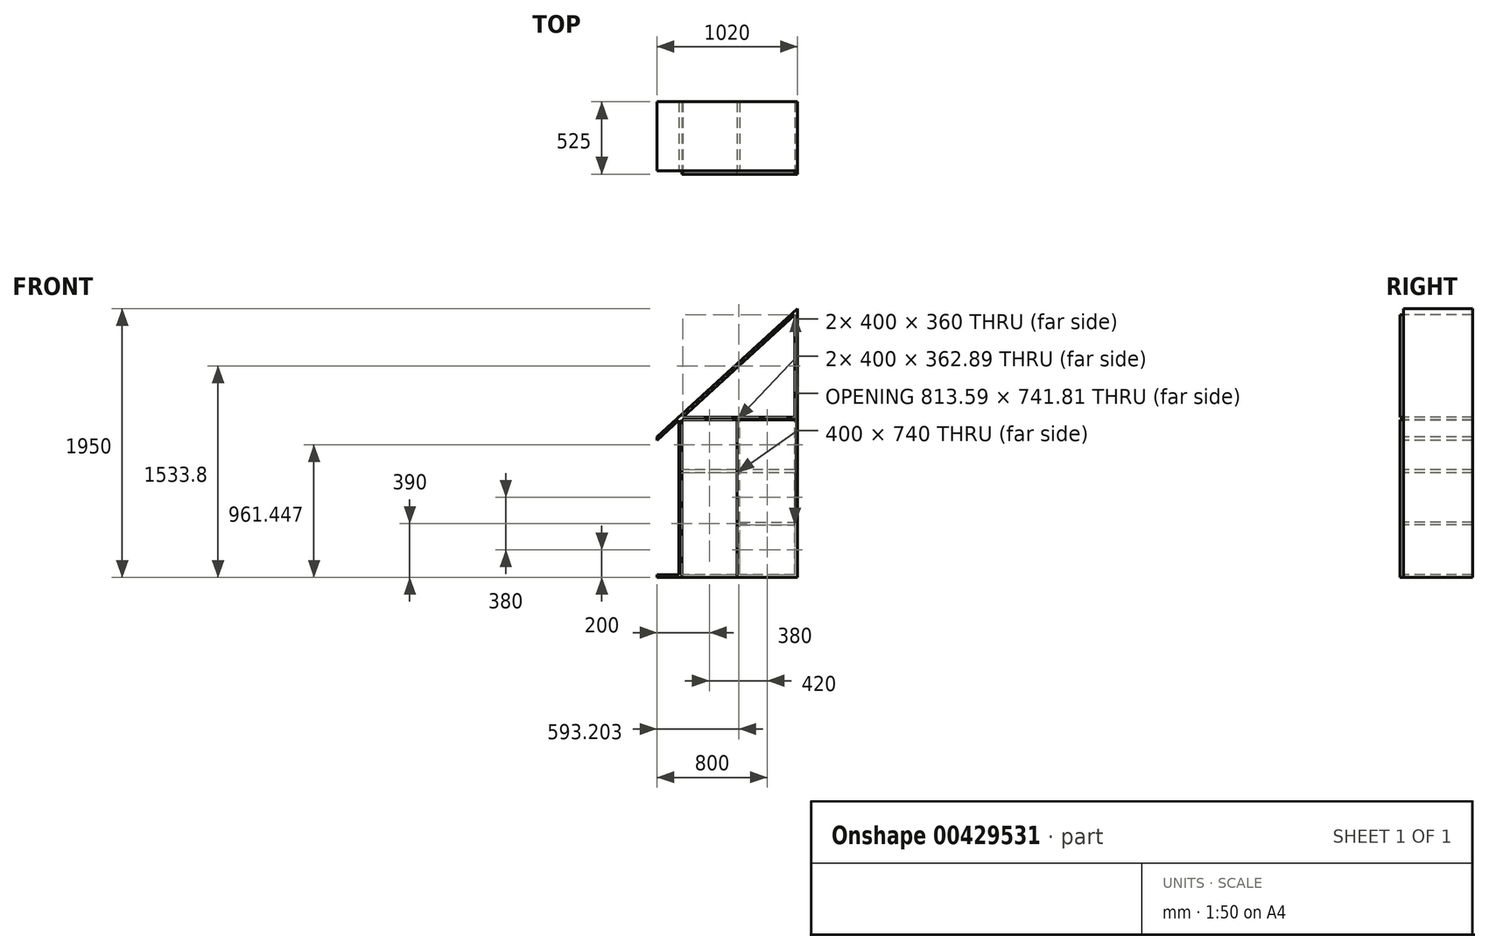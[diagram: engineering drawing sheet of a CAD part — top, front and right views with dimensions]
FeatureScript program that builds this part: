
annotation { "Feature Type Name" : "Feature", "Feature Type Description" : "" }
export const myFeature = defineFeature(function(context is Context, id is Id, definition is map)
    precondition{}
    {
        {
            var Q0;
            Q0=qCreatedBy(makeId("Front.planeOp"),FACE);
            var sketch = newSketch(context, id + "F0", { "sketchPlane" : qUnion([Q0])});
            skLineSegment(sketch, "E0.bottom", {"start": v(510, -975) * mm, "end": v(-510, -975) * mm});
            skLineSegment(sketch, "E0.left", {"start": v(510, -975) * mm, "end": v(510, 975) * mm});
            skLineSegment(sketch, "E0.right", {"start": v(-510, -975) * mm, "end": v(-510, 45) * mm});
            skPoint(sketch, "E0.middle", {"position": v(0, 180) * mm});
            skLineSegment(sketch, "E1", {"start": v(-510, 45) * mm, "end": v(510, 975) * mm});
            skLineSegment(sketch, "E2.0", {"start": v(-350, -975) * mm, "end": v(-350, 190.88) * mm});
            skPoint(sketch, "E0.top.end.orphan", {"position": v(-510, 975) * mm});
            skLineSegment(sketch, "E3", {"start": v(-350, 167.9) * mm, "end": v(70, 167.9) * mm});
            skLineSegment(sketch, "E4.0", {"start": v(510, -215) * mm, "end": v(90, -215) * mm});
            skLineSegment(sketch, "E5.0", {"start": v(510, -955) * mm, "end": v(-510, -955) * mm});
            skLineSegment(sketch, "E6.0", {"start": v(-330, -975) * mm, "end": v(-330, 209.12) * mm});
            skLineSegment(sketch, "E7.0", {"start": v(510, -195) * mm, "end": v(90, -195) * mm});
            skLineSegment(sketch, "E8.0", {"start": v(-510, 17.93) * mm, "end": v(510, 947.93) * mm});
            skLineSegment(sketch, "E9.0", {"start": v(90, -975) * mm, "end": v(90, -595) * mm});
            skLineSegment(sketch, "E10.0", {"start": v(70, -975) * mm, "end": v(70, 187.9) * mm});
            skLineSegment(sketch, "E11.0", {"start": v(-330, 187.9) * mm, "end": v(70, 187.9) * mm});
            skLineSegment(sketch, "E12.0", {"start": v(490, -975) * mm, "end": v(490, -595) * mm});
            skLineSegment(sketch, "E13.trimOffspring", {"start": v(70, -195) * mm, "end": v(-350, -195) * mm});
            skLineSegment(sketch, "E14.trimOffspring", {"start": v(70, -215) * mm, "end": v(-350, -215) * mm});
            skLineSegment(sketch, "E15.trimOffspring", {"start": v(90, 187.9) * mm, "end": v(510, 187.9) * mm});
            skLineSegment(sketch, "E16.trimOffspring", {"start": v(90, 167.9) * mm, "end": v(510, 167.9) * mm});
            skLineSegment(sketch, "E17", {"start": v(70, 167.9) * mm, "end": v(90, 167.9) * mm});
            skLineSegment(sketch, "E18", {"start": v(70, 187.9) * mm, "end": v(90, 187.9) * mm});
            skLineSegment(sketch, "E19", {"start": v(90, -575) * mm, "end": v(490, -575) * mm});
            skLineSegment(sketch, "E20", {"start": v(90, -595) * mm, "end": v(490, -595) * mm});
            skLineSegment(sketch, "E21.trimOffspring", {"start": v(90, -575) * mm, "end": v(90, 187.9) * mm});
            skLineSegment(sketch, "E22.trimOffspring", {"start": v(490, -575) * mm, "end": v(490, 956.76) * mm});
            skSolve(sketch);
        }
        {
            var Q0;
            {var subQ0=sQuery(id+"F0.wireOp",EDGE,"E6.0");var subQ1=sQuery(id+"F0.wireOp",EDGE,"E0.bottom");var subQ2=makeQuery(id+"F0.imprint","INTERSECT",VERTEX,{"derivedFrom":[subQ1,subQ0]});Q0=makeQuery(id+"F0.imprint","IMPRINT",FACE,{"disambiguationData":[TD([[makeQuery(id+"F0.imprint","IMPRINT",EDGE,{"disambiguationData":[TD([[subQ2,1.0]])],"derivedFrom":subQ1}),-1.0]])]});}
            var Q1;
            {var subQ0=sQuery(id+"F0.wireOp",EDGE,"E10.0");var subQ1=sQuery(id+"F0.wireOp",EDGE,"6faa854c-3392-4649-b0cb-d51412c366a2.0");var subQ2=makeQuery(id+"F0.imprint","INTERSECT",VERTEX,{"derivedFrom":[subQ1,subQ0]});Q1=makeQuery(id+"F0.imprint","IMPRINT",FACE,{"disambiguationData":[TD([[makeQuery(id+"F0.imprint","IMPRINT",EDGE,{"disambiguationData":[TD([[subQ2,-1.0]])],"derivedFrom":subQ1}),1.0]])]});}
            var Q2;
            {var subQ0=sQuery(id+"F0.wireOp",EDGE,"E10.0");var subQ1=sQuery(id+"F0.wireOp",EDGE,"6faa854c-3392-4649-b0cb-d51412c366a2.0");var subQ2=makeQuery(id+"F0.imprint","INTERSECT",VERTEX,{"derivedFrom":[subQ1,subQ0]});Q2=makeQuery(id+"F0.imprint","IMPRINT",FACE,{"disambiguationData":[TD([[makeQuery(id+"F0.imprint","IMPRINT",EDGE,{"disambiguationData":[TD([[subQ2,-1.0]])],"derivedFrom":subQ1}),-1.0]])]});}
            var Q3;
            {var subQ0=sQuery(id+"F0.wireOp",EDGE,"b3576428-8442-4fca-9c3f-cbccb2f376bd.0");var subQ1=sQuery(id+"F0.wireOp",EDGE,"E6.0");var subQ2=makeQuery(id+"F0.imprint","INTERSECT",VERTEX,{"derivedFrom":[subQ1,subQ0]});Q3=makeQuery(id+"F0.imprint","IMPRINT",FACE,{"disambiguationData":[TD([[makeQuery(id+"F0.imprint","IMPRINT",EDGE,{"disambiguationData":[TD([[subQ2,-1.0]])],"derivedFrom":subQ1}),-1.0]])]});}
            var Q4;
            {var subQ2=sQuery(id+"F0.wireOp",EDGE,"a34f5626-0c33-47cb-b1fa-9412c36bbc4b.0");var subQ8=sQuery(id+"F0.wireOp",EDGE,"E10.0");var subQ9=makeQuery(id+"F0.imprint","INTERSECT",VERTEX,{"derivedFrom":[subQ2,subQ8]});Q4=makeQuery(id+"F0.imprint","IMPRINT",FACE,{"disambiguationData":[TD([[makeQuery(id+"F0.imprint","IMPRINT",EDGE,{"disambiguationData":[TD([[subQ9,-1.0]])],"derivedFrom":subQ2}),-1.0]])]});}
            var Q5;
            {var subQ0=sQuery(id+"F0.wireOp",EDGE,"E10.0");var subQ1=sQuery(id+"F0.wireOp",EDGE,"E3");var subQ2=makeQuery(id+"F0.imprint","INTERSECT",VERTEX,{"derivedFrom":[subQ1,subQ0]});Q5=makeQuery(id+"F0.imprint","IMPRINT",FACE,{"disambiguationData":[TD([[makeQuery(id+"F0.imprint","IMPRINT",EDGE,{"disambiguationData":[TD([[subQ2,1.0]])],"derivedFrom":subQ1}),-1.0]])]});}
            var Q6;
            {var subQ0=sQuery(id+"F0.wireOp",EDGE,"E14.trimOffspring");var subQ1=sQuery(id+"F0.wireOp",EDGE,"E6.0");var subQ2=makeQuery(id+"F0.imprint","INTERSECT",VERTEX,{"derivedFrom":[subQ1,subQ0]});Q6=makeQuery(id+"F0.imprint","IMPRINT",FACE,{"disambiguationData":[TD([[makeQuery(id+"F0.imprint","IMPRINT",EDGE,{"disambiguationData":[TD([[subQ2,-1.0]])],"derivedFrom":subQ1}),-1.0]])]});}
            var Q7;
            {var subQ0=sQuery(id+"F0.wireOp",EDGE,"E10.0");var subQ1=sQuery(id+"F0.wireOp",EDGE,"E5.0");var subQ2=makeQuery(id+"F0.imprint","INTERSECT",VERTEX,{"derivedFrom":[subQ1,subQ0]});Q7=makeQuery(id+"F0.imprint","IMPRINT",FACE,{"disambiguationData":[TD([[makeQuery(id+"F0.imprint","IMPRINT",EDGE,{"disambiguationData":[TD([[subQ2,-1.0]])],"derivedFrom":subQ1}),-1.0]])]});}
            extrude(context, id + "F1", {"entities" : qUnion([Q0, Q1, Q2, Q3, Q4, Q5, Q6, Q7]), "depth" : 25 * mm});
        }
        {
            var Q0;
            {var subQ0=sQuery(id+"F0.wireOp",EDGE,"E9.0");var subQ1=sQuery(id+"F0.wireOp",EDGE,"E0.bottom");var subQ2=makeQuery(id+"F0.imprint","INTERSECT",VERTEX,{"derivedFrom":[subQ1,subQ0]});Q0=makeQuery(id+"F0.imprint","IMPRINT",FACE,{"disambiguationData":[TD([[makeQuery(id+"F0.imprint","IMPRINT",EDGE,{"disambiguationData":[TD([[subQ2,1.0]])],"derivedFrom":subQ1}),-1.0]])]});}
            var Q1;
            {var subQ0=sQuery(id+"F0.wireOp",EDGE,"E9.0");var subQ1=sQuery(id+"F0.wireOp",EDGE,"E4.0");var subQ2=makeQuery(id+"F0.imprint","INTERSECT",VERTEX,{"derivedFrom":[subQ1,subQ0]});Q1=makeQuery(id+"F0.imprint","IMPRINT",FACE,{"disambiguationData":[TD([[makeQuery(id+"F0.imprint","IMPRINT",EDGE,{"disambiguationData":[TD([[subQ2,1.0]])],"derivedFrom":subQ1}),1.0]])]});}
            var Q2;
            {var subQ0=sQuery(id+"F0.wireOp",EDGE,"E9.0");var subQ1=sQuery(id+"F0.wireOp",EDGE,"E7.0");var subQ2=makeQuery(id+"F0.imprint","INTERSECT",VERTEX,{"derivedFrom":[subQ1,subQ0]});Q2=makeQuery(id+"F0.imprint","IMPRINT",FACE,{"disambiguationData":[TD([[makeQuery(id+"F0.imprint","IMPRINT",EDGE,{"disambiguationData":[TD([[subQ2,1.0]])],"derivedFrom":subQ1}),-1.0]])]});}
            var Q3;
            {var subQ0=sQuery(id+"F0.wireOp",EDGE,"E9.0");var subQ1=sQuery(id+"F0.wireOp",EDGE,"E4.0");var subQ2=makeQuery(id+"F0.imprint","INTERSECT",VERTEX,{"derivedFrom":[subQ1,subQ0]});Q3=makeQuery(id+"F0.imprint","IMPRINT",FACE,{"disambiguationData":[TD([[makeQuery(id+"F0.imprint","IMPRINT",EDGE,{"disambiguationData":[TD([[subQ2,1.0]])],"derivedFrom":subQ1}),-1.0]])]});}
            var Q4;
            {var subQ0=sQuery(id+"F0.wireOp",EDGE,"E17");Q4=makeQuery(id+"F0.imprint","IMPRINT",FACE,{"disambiguationData":[TD([[makeQuery(id+"F0.imprint","IMPRINT",EDGE,{"derivedFrom":subQ0}),-1.0]])]});}
            var Q5;
            {var subQ5=sQuery(id+"F0.wireOp",EDGE,"E20");Q5=makeQuery(id+"F0.imprint","IMPRINT",FACE,{"disambiguationData":[TD([[makeQuery(id+"F0.imprint","IMPRINT",EDGE,{"derivedFrom":subQ5}),-1.0]])]});}
            var Q6;
            {var subQ0=sQuery(id+"F0.wireOp",EDGE,"E9.0");var subQ1=sQuery(id+"F0.wireOp",EDGE,"E0.bottom");var subQ2=makeQuery(id+"F0.imprint","INTERSECT",VERTEX,{"derivedFrom":[subQ1,subQ0]});Q6=makeQuery(id+"F0.imprint","IMPRINT",FACE,{"disambiguationData":[TD([[makeQuery(id+"F0.imprint","IMPRINT",EDGE,{"disambiguationData":[TD([[subQ2,-1.0]])],"derivedFrom":subQ1}),-1.0]])]});}
            var Q7;
            {var subQ0=sQuery(id+"F0.wireOp",EDGE,"E0.left");var subQ1=sQuery(id+"F0.wireOp",EDGE,"E0.bottom");var subQ2=makeQuery(id+"F0.imprint","INTERSECT",VERTEX,{"derivedFrom":[subQ1,subQ0]});Q7=makeQuery(id+"F0.imprint","IMPRINT",FACE,{"disambiguationData":[TD([[makeQuery(id+"F0.imprint","IMPRINT",EDGE,{"disambiguationData":[TD([[subQ2,-1.0]])],"derivedFrom":subQ1}),-1.0]])]});}
            extrude(context, id + "F2", {"entities" : qUnion([Q0, Q1, Q2, Q3, Q4, Q5, Q6, Q7]), "depth" : 25 * mm});
        }
        {
            var Q0;
            {var subQ0=sQuery(id+"F0.wireOp",EDGE,"E9.0");var subQ1=sQuery(id+"F0.wireOp",EDGE,"E0.bottom");var subQ2=makeQuery(id+"F0.imprint","INTERSECT",VERTEX,{"derivedFrom":[subQ1,subQ0]});Q0=makeQuery(id+"F0.imprint","IMPRINT",FACE,{"disambiguationData":[TD([[makeQuery(id+"F0.imprint","IMPRINT",EDGE,{"disambiguationData":[TD([[subQ2,1.0]])],"derivedFrom":subQ1}),-1.0]])]});}
            var Q1;
            {var subQ0=sQuery(id+"F0.wireOp",EDGE,"E8.0");var subQ1=sQuery(id+"F0.wireOp",EDGE,"E0.left");var subQ2=makeQuery(id+"F0.imprint","INTERSECT",VERTEX,{"derivedFrom":[subQ1,subQ0]});Q1=makeQuery(id+"F0.imprint","IMPRINT",FACE,{"disambiguationData":[TD([[makeQuery(id+"F0.imprint","IMPRINT",EDGE,{"disambiguationData":[TD([[subQ2,1.0]])],"derivedFrom":subQ1}),1.0]])]});}
            var Q2;
            {var subQ1=sQuery(id+"F0.wireOp",EDGE,"E6.0");var subQ7=sQuery(id+"F0.wireOp",EDGE,"E1");var subQ8=makeQuery(id+"F0.imprint","INTERSECT",VERTEX,{"derivedFrom":[subQ7,subQ1]});Q2=makeQuery(id+"F0.imprint","IMPRINT",FACE,{"disambiguationData":[TD([[makeQuery(id+"F0.imprint","IMPRINT",EDGE,{"disambiguationData":[TD([[subQ8,-1.0]])],"derivedFrom":subQ7}),-1.0]])]});}
            var Q3;
            {var subQ0=sQuery(id+"F0.wireOp",EDGE,"E15.trimOffspring");var subQ1=sQuery(id+"F0.wireOp",EDGE,"E0.left");var subQ2=makeQuery(id+"F0.imprint","INTERSECT",VERTEX,{"derivedFrom":[subQ1,subQ0]});Q3=makeQuery(id+"F0.imprint","IMPRINT",FACE,{"disambiguationData":[TD([[makeQuery(id+"F0.imprint","IMPRINT",EDGE,{"disambiguationData":[TD([[subQ2,1.0]])],"derivedFrom":subQ1}),1.0]])]});}
            var Q4;
            {var subQ0=sQuery(id+"F0.wireOp",EDGE,"E17");Q4=makeQuery(id+"F0.imprint","IMPRINT",FACE,{"disambiguationData":[TD([[makeQuery(id+"F0.imprint","IMPRINT",EDGE,{"derivedFrom":subQ0}),1.0]])]});}
            var Q5;
            {var subQ1=sQuery(id+"F0.wireOp",EDGE,"E6.0");var subQ7=sQuery(id+"F0.wireOp",EDGE,"E3");var subQ8=makeQuery(id+"F0.imprint","INTERSECT",VERTEX,{"derivedFrom":[subQ7,subQ1]});Q5=makeQuery(id+"F0.imprint","IMPRINT",FACE,{"disambiguationData":[TD([[makeQuery(id+"F0.imprint","IMPRINT",EDGE,{"disambiguationData":[TD([[subQ8,-1.0]])],"derivedFrom":subQ1}),-1.0]])]});}
            var Q6;
            {var subQ1=sQuery(id+"F0.wireOp",EDGE,"E2.0");var subQ7=sQuery(id+"F0.wireOp",EDGE,"E1");var subQ8=makeQuery(id+"F0.imprint","INTERSECT",VERTEX,{"derivedFrom":[subQ7,subQ1]});Q6=makeQuery(id+"F0.imprint","IMPRINT",FACE,{"disambiguationData":[TD([[makeQuery(id+"F0.imprint","IMPRINT",EDGE,{"disambiguationData":[TD([[subQ8,-1.0]])],"derivedFrom":subQ7}),-1.0]])]});}
            var Q7;
            {var subQ0=sQuery(id+"F0.wireOp",EDGE,"E8.0");var subQ1=sQuery(id+"F0.wireOp",EDGE,"E3");var subQ2=makeQuery(id+"F0.imprint","INTERSECT",VERTEX,{"derivedFrom":[subQ1,subQ0]});Q7=makeQuery(id+"F0.imprint","IMPRINT",FACE,{"disambiguationData":[TD([[makeQuery(id+"F0.imprint","IMPRINT",EDGE,{"disambiguationData":[TD([[subQ2,-1.0]])],"derivedFrom":subQ1}),1.0]])]});}
            var Q8;
            {var subQ0=sQuery(id+"F0.wireOp",EDGE,"E11.0");var subQ1=sQuery(id+"F0.wireOp",EDGE,"E6.0");var subQ2=makeQuery(id+"F0.imprint","INTERSECT",VERTEX,{"derivedFrom":[subQ1,subQ0]});Q8=makeQuery(id+"F0.imprint","IMPRINT",FACE,{"disambiguationData":[TD([[makeQuery(id+"F0.imprint","IMPRINT",EDGE,{"disambiguationData":[TD([[subQ2,1.0]])],"derivedFrom":subQ1}),-1.0]])]});}
            var Q9;
            {var subQ0=sQuery(id+"F0.wireOp",EDGE,"E3");var subQ1=sQuery(id+"F0.wireOp",EDGE,"E2.0");var subQ2=makeQuery(id+"F0.imprint","INTERSECT",VERTEX,{"derivedFrom":[subQ1,subQ0]});Q9=makeQuery(id+"F0.imprint","IMPRINT",FACE,{"disambiguationData":[TD([[makeQuery(id+"F0.imprint","IMPRINT",EDGE,{"disambiguationData":[TD([[subQ2,1.0]])],"derivedFrom":subQ1}),-1.0]])]});}
            var Q10;
            {var subQ4=sQuery(id+"F0.wireOp",EDGE,"E0.right");var subQ6=sQuery(id+"F0.wireOp",EDGE,"E1");var subQ7=makeQuery(id+"F0.imprint","INTERSECT",VERTEX,{"derivedFrom":[subQ4,subQ6]});Q10=makeQuery(id+"F0.imprint","IMPRINT",FACE,{"disambiguationData":[TD([[makeQuery(id+"F0.imprint","IMPRINT",EDGE,{"disambiguationData":[TD([[subQ7,1.0]])],"derivedFrom":subQ4}),-1.0]])]});}
            var Q11;
            {var subQ3=sQuery(id+"F0.wireOp",EDGE,"E13.trimOffspring");var subQ6=sQuery(id+"F0.wireOp",EDGE,"E2.0");var subQ9=makeQuery(id+"F0.imprint","INTERSECT",VERTEX,{"derivedFrom":[subQ6,subQ3]});Q11=makeQuery(id+"F0.imprint","IMPRINT",FACE,{"disambiguationData":[TD([[makeQuery(id+"F0.imprint","IMPRINT",EDGE,{"disambiguationData":[TD([[subQ9,-1.0]])],"derivedFrom":subQ6}),-1.0]])]});}
            var Q12;
            {var subQ0=sQuery(id+"F0.wireOp",EDGE,"E17");Q12=makeQuery(id+"F0.imprint","IMPRINT",FACE,{"disambiguationData":[TD([[makeQuery(id+"F0.imprint","IMPRINT",EDGE,{"derivedFrom":subQ0}),-1.0]])]});}
            var Q13;
            {var subQ0=sQuery(id+"F0.wireOp",EDGE,"E4.0");var subQ1=sQuery(id+"F0.wireOp",EDGE,"E0.left");var subQ2=makeQuery(id+"F0.imprint","INTERSECT",VERTEX,{"derivedFrom":[subQ1,subQ0]});Q13=makeQuery(id+"F0.imprint","IMPRINT",FACE,{"disambiguationData":[TD([[makeQuery(id+"F0.imprint","IMPRINT",EDGE,{"disambiguationData":[TD([[subQ2,-1.0]])],"derivedFrom":subQ1}),1.0]])]});}
            var Q14;
            {var subQ0=sQuery(id+"F0.wireOp",EDGE,"E21.trimOffspring");var subQ1=sQuery(id+"F0.wireOp",EDGE,"E4.0");var subQ2=makeQuery(id+"F0.imprint","INTERSECT",VERTEX,{"derivedFrom":[subQ1,subQ0]});Q14=makeQuery(id+"F0.imprint","IMPRINT",FACE,{"disambiguationData":[TD([[makeQuery(id+"F0.imprint","IMPRINT",EDGE,{"disambiguationData":[TD([[subQ2,1.0]])],"derivedFrom":subQ1}),-1.0]])]});}
            var Q15;
            {var subQ0=sQuery(id+"F0.wireOp",EDGE,"E14.trimOffspring");var subQ1=sQuery(id+"F0.wireOp",EDGE,"E6.0");var subQ2=makeQuery(id+"F0.imprint","INTERSECT",VERTEX,{"derivedFrom":[subQ1,subQ0]});Q15=makeQuery(id+"F0.imprint","IMPRINT",FACE,{"disambiguationData":[TD([[makeQuery(id+"F0.imprint","IMPRINT",EDGE,{"disambiguationData":[TD([[subQ2,-1.0]])],"derivedFrom":subQ1}),-1.0]])]});}
            var Q16;
            {var subQ0=sQuery(id+"F0.wireOp",EDGE,"E7.0");var subQ1=sQuery(id+"F0.wireOp",EDGE,"E0.left");var subQ2=makeQuery(id+"F0.imprint","INTERSECT",VERTEX,{"derivedFrom":[subQ1,subQ0]});Q16=makeQuery(id+"F0.imprint","IMPRINT",FACE,{"disambiguationData":[TD([[makeQuery(id+"F0.imprint","IMPRINT",EDGE,{"disambiguationData":[TD([[subQ2,-1.0]])],"derivedFrom":subQ1}),1.0]])]});}
            var Q17;
            {var subQ0=sQuery(id+"F0.wireOp",EDGE,"E4.0");var subQ1=sQuery(id+"F0.wireOp",EDGE,"E0.left");var subQ2=makeQuery(id+"F0.imprint","INTERSECT",VERTEX,{"derivedFrom":[subQ1,subQ0]});Q17=makeQuery(id+"F0.imprint","IMPRINT",FACE,{"disambiguationData":[TD([[makeQuery(id+"F0.imprint","IMPRINT",EDGE,{"disambiguationData":[TD([[subQ2,-1.0]])],"derivedFrom":subQ1}),1.0]])]});}
            var Q18;
            {var subQ0=sQuery(id+"F0.wireOp",EDGE,"E17");Q18=makeQuery(id+"F0.imprint","IMPRINT",FACE,{"disambiguationData":[TD([[makeQuery(id+"F0.imprint","IMPRINT",EDGE,{"derivedFrom":subQ0}),-1.0]])]});}
            var Q19;
            {var subQ0=sQuery(id+"F0.wireOp",EDGE,"E13.trimOffspring");var subQ1=sQuery(id+"F0.wireOp",EDGE,"E2.0");var subQ2=makeQuery(id+"F0.imprint","INTERSECT",VERTEX,{"derivedFrom":[subQ1,subQ0]});Q19=makeQuery(id+"F0.imprint","IMPRINT",FACE,{"disambiguationData":[TD([[makeQuery(id+"F0.imprint","IMPRINT",EDGE,{"disambiguationData":[TD([[subQ2,1.0]])],"derivedFrom":subQ1}),-1.0]])]});}
            var Q20;
            {var subQ0=sQuery(id+"F0.wireOp",EDGE,"E3");var subQ1=sQuery(id+"F0.wireOp",EDGE,"E2.0");var subQ2=makeQuery(id+"F0.imprint","INTERSECT",VERTEX,{"derivedFrom":[subQ1,subQ0]});Q20=makeQuery(id+"F0.imprint","IMPRINT",FACE,{"disambiguationData":[TD([[makeQuery(id+"F0.imprint","IMPRINT",EDGE,{"disambiguationData":[TD([[subQ2,1.0]])],"derivedFrom":subQ1}),-1.0]])]});}
            var Q21;
            {var subQ0=sQuery(id+"F0.wireOp",EDGE,"E3");var subQ1=sQuery(id+"F0.wireOp",EDGE,"E2.0");var subQ2=makeQuery(id+"F0.imprint","INTERSECT",VERTEX,{"derivedFrom":[subQ1,subQ0]});Q21=makeQuery(id+"F0.imprint","IMPRINT",FACE,{"disambiguationData":[TD([[makeQuery(id+"F0.imprint","IMPRINT",EDGE,{"disambiguationData":[TD([[subQ2,1.0]])],"derivedFrom":subQ1}),-1.0]])]});}
            var Q22;
            {var subQ0=sQuery(id+"F0.wireOp",EDGE,"E3");var subQ1=sQuery(id+"F0.wireOp",EDGE,"E2.0");var subQ2=makeQuery(id+"F0.imprint","INTERSECT",VERTEX,{"derivedFrom":[subQ1,subQ0]});Q22=makeQuery(id+"F0.imprint","IMPRINT",FACE,{"disambiguationData":[TD([[makeQuery(id+"F0.imprint","IMPRINT",EDGE,{"disambiguationData":[TD([[subQ2,1.0]])],"derivedFrom":subQ1}),-1.0]])]});}
            var Q23;
            {var subQ0=sQuery(id+"F0.wireOp",EDGE,"E2.0");var subQ1=sQuery(id+"F0.wireOp",EDGE,"E0.bottom");var subQ2=makeQuery(id+"F0.imprint","INTERSECT",VERTEX,{"derivedFrom":[subQ1,subQ0]});Q23=makeQuery(id+"F0.imprint","IMPRINT",FACE,{"disambiguationData":[TD([[makeQuery(id+"F0.imprint","IMPRINT",EDGE,{"disambiguationData":[TD([[subQ2,1.0]])],"derivedFrom":subQ1}),-1.0]])]});}
            var Q24;
            {var subQ0=sQuery(id+"F0.wireOp",EDGE,"E6.0");var subQ1=sQuery(id+"F0.wireOp",EDGE,"E0.bottom");var subQ2=makeQuery(id+"F0.imprint","INTERSECT",VERTEX,{"derivedFrom":[subQ1,subQ0]});Q24=makeQuery(id+"F0.imprint","IMPRINT",FACE,{"disambiguationData":[TD([[makeQuery(id+"F0.imprint","IMPRINT",EDGE,{"disambiguationData":[TD([[subQ2,1.0]])],"derivedFrom":subQ1}),-1.0]])]});}
            var Q25;
            {var subQ0=sQuery(id+"F0.wireOp",EDGE,"E9.0");var subQ1=sQuery(id+"F0.wireOp",EDGE,"E0.bottom");var subQ2=makeQuery(id+"F0.imprint","INTERSECT",VERTEX,{"derivedFrom":[subQ1,subQ0]});Q25=makeQuery(id+"F0.imprint","IMPRINT",FACE,{"disambiguationData":[TD([[makeQuery(id+"F0.imprint","IMPRINT",EDGE,{"disambiguationData":[TD([[subQ2,-1.0]])],"derivedFrom":subQ1}),-1.0]])]});}
            var Q26;
            {var subQ0=sQuery(id+"F0.wireOp",EDGE,"E9.0");var subQ1=sQuery(id+"F0.wireOp",EDGE,"E0.bottom");var subQ2=makeQuery(id+"F0.imprint","INTERSECT",VERTEX,{"derivedFrom":[subQ1,subQ0]});Q26=makeQuery(id+"F0.imprint","IMPRINT",FACE,{"disambiguationData":[TD([[makeQuery(id+"F0.imprint","IMPRINT",EDGE,{"disambiguationData":[TD([[subQ2,1.0]])],"derivedFrom":subQ1}),-1.0]])]});}
            var Q27;
            {var subQ0=sQuery(id+"F0.wireOp",EDGE,"E0.left");var subQ1=sQuery(id+"F0.wireOp",EDGE,"E0.bottom");var subQ2=makeQuery(id+"F0.imprint","INTERSECT",VERTEX,{"derivedFrom":[subQ1,subQ0]});Q27=makeQuery(id+"F0.imprint","IMPRINT",FACE,{"disambiguationData":[TD([[makeQuery(id+"F0.imprint","IMPRINT",EDGE,{"disambiguationData":[TD([[subQ2,-1.0]])],"derivedFrom":subQ1}),-1.0]])]});}
            var Q28;
            {var subQ0=sQuery(id+"F0.wireOp",EDGE,"E0.right");var subQ1=sQuery(id+"F0.wireOp",EDGE,"E0.bottom");var subQ2=makeQuery(id+"F0.imprint","INTERSECT",VERTEX,{"derivedFrom":[subQ1,subQ0]});Q28=makeQuery(id+"F0.imprint","IMPRINT",FACE,{"disambiguationData":[TD([[makeQuery(id+"F0.imprint","IMPRINT",EDGE,{"disambiguationData":[TD([[subQ2,1.0]])],"derivedFrom":subQ1}),-1.0]])]});}
            var Q29;
            {var subQ0=sQuery(id+"F0.wireOp",EDGE,"E1");var subQ1=sQuery(id+"F0.wireOp",EDGE,"E0.left");var subQ2=makeQuery(id+"F0.imprint","INTERSECT",VERTEX,{"derivedFrom":[subQ1,subQ0]});Q29=makeQuery(id+"F0.imprint","IMPRINT",FACE,{"disambiguationData":[TD([[makeQuery(id+"F0.imprint","IMPRINT",EDGE,{"disambiguationData":[TD([[subQ2,1.0]])],"derivedFrom":subQ1}),1.0]])]});}
            var Q30;
            {var subQ1=sQuery(id+"F0.wireOp",EDGE,"E15.trimOffspring");var subQ3=sQuery(id+"F0.wireOp",EDGE,"E22.trimOffspring");var subQ4=makeQuery(id+"F0.imprint","INTERSECT",VERTEX,{"derivedFrom":[subQ1,subQ3]});Q30=makeQuery(id+"F0.imprint","IMPRINT",FACE,{"disambiguationData":[TD([[makeQuery(id+"F0.imprint","IMPRINT",EDGE,{"disambiguationData":[TD([[subQ4,1.0]])],"derivedFrom":subQ3}),1.0]])]});}
            var Q31;
            {var subQ0=sQuery(id+"F0.wireOp",EDGE,"E14.trimOffspring");var subQ1=sQuery(id+"F0.wireOp",EDGE,"E2.0");var subQ2=makeQuery(id+"F0.imprint","INTERSECT",VERTEX,{"derivedFrom":[subQ1,subQ0]});Q31=makeQuery(id+"F0.imprint","IMPRINT",FACE,{"disambiguationData":[TD([[makeQuery(id+"F0.imprint","IMPRINT",EDGE,{"disambiguationData":[TD([[subQ2,1.0]])],"derivedFrom":subQ1}),-1.0]])]});}
            extrude(context, id + "F3", {"entities" : qUnion([Q0, Q1, Q2, Q3, Q4, Q5, Q6, Q7, Q8, Q9, Q10, Q11, Q12, Q13, Q14, Q15, Q16, Q17, Q18, Q19, Q20, Q21, Q22, Q23, Q24, Q25, Q26, Q27, Q28, Q29, Q30, Q31]), "oppositeDirection" : true, "depth" : 500 * mm});
        }
        {
            var Q0;
            {var subQ0=sQuery(id+"F0.wireOp",EDGE,"E18");Q0=makeQuery(id+"F0.imprint","IMPRINT",FACE,{"disambiguationData":[TD([[makeQuery(id+"F0.imprint","IMPRINT",EDGE,{"derivedFrom":subQ0}),1.0]])]});}
            var Q1;
            {var subQ3=sQuery(id+"F0.wireOp",EDGE,"E16.trimOffspring");var subQ5=sQuery(id+"F0.wireOp",EDGE,"E12.0");var subQ6=makeQuery(id+"F0.imprint","INTERSECT",VERTEX,{"derivedFrom":[subQ5,subQ3]});Q1=makeQuery(id+"F0.imprint","IMPRINT",FACE,{"disambiguationData":[TD([[makeQuery(id+"F0.imprint","IMPRINT",EDGE,{"disambiguationData":[TD([[subQ6,-1.0]])],"derivedFrom":subQ5}),1.0]])]});}
            extrude(context, id + "F4", {"entities" : qUnion([Q0, Q1]), "depth" : 25 * mm});
        }
        {
            var Q0;
            Q0=makeQuery(id+"F4.opExtrude","SWEPT_BODY",BODY,{"disambiguationData":[OSD([sQuery(id+"F0.wireOp",EDGE,"E0.bottom"),sQuery(id+"F0.wireOp",EDGE,"E9.0"),sQuery(id+"F0.wireOp",EDGE,"E12.0"),sQuery(id+"F0.wireOp",EDGE,"E20")])]});
            deleteBodies(context, id + "F5", {"entities" : qUnion([Q0])});
        }
        {
            var Q0;
            Q0=makeQuery(id+"F1.opExtrude","SWEPT_BODY",BODY,{"disambiguationData":[OSD([sQuery(id+"F0.wireOp",EDGE,"E6.0"),sQuery(id+"F0.wireOp",EDGE,"E8.0"),sQuery(id+"F0.wireOp",EDGE,"E11.0")])]});
            deleteBodies(context, id + "F6", {"entities" : qUnion([Q0])});
        }
    });
